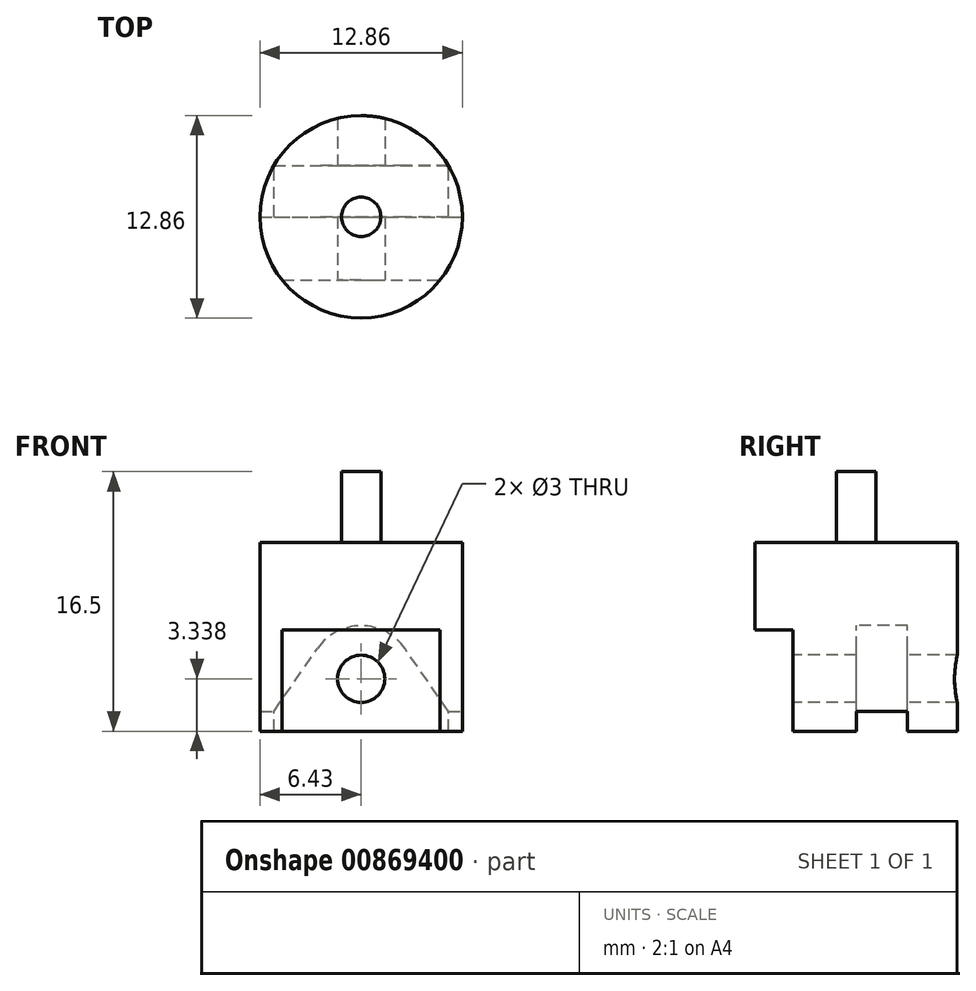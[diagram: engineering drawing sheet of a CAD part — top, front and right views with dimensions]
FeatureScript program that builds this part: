
annotation { "Feature Type Name" : "Feature", "Feature Type Description" : "" }
export const myFeature = defineFeature(function(context is Context, id is Id, definition is map)
    precondition{}
    {
        {
            var Q0;
            Q0=qCreatedBy(makeId("Top.planeOp"),FACE);
            var sketch = newSketch(context, id + "F0", { "sketchPlane" : qUnion([Q0])});
            skCircle(sketch, "E0", {"center": v(0, 0) * mm, "radius": 6.42 * mm});
            skSolve(sketch);
        }
        {
            var Q0;
            Q0=qSketchRegion(id+"F0",true);
            extrude(context, id + "F1", {"entities" : qUnion([Q0]), "oppositeDirection" : true, "depth" : 12 * mm, "offsetDistance" : 25 * mm});
        }
        {
            var Q0;
            Q0=qCreatedBy(makeId("Front.planeOp"),FACE);
            var sketch = newSketch(context, id + "F2", { "sketchPlane" : qUnion([Q0])});
            skCircle(sketch, "E1", {"center": v(0, -8.66) * mm, "radius": 1.5 * mm});
            skSolve(sketch);
        }
        {
            var Q0;
            Q0=qSketchRegion(id+"F2",true);
            extrude(context, id + "F3", {"entities" : qUnion([Q0]), "operationType" : NewBodyOperationType.REMOVE, "endBound" : BoundingType.SYMMETRIC, "oppositeDirection" : true, "depth" : 25 * mm, "offsetDistance" : 25 * mm});
        }
        {
            var Q0;
            Q0=qCreatedBy(makeId("Front.planeOp"),FACE);
            var sketch = newSketch(context, id + "F4", { "sketchPlane" : qUnion([Q0])});
            skArc(sketch, "E2", {"start": v(2.77, -6.74) * mm, "mid": v(0, -5.29) * mm, "end": v(-2.77, -6.74) * mm});
            skLineSegment(sketch, "E3.0", {"start": v(-6.42, -12) * mm, "end": v(6.42, -12) * mm});
            skLineSegment(sketch, "E4", {"start": v(6.43, -12) * mm, "end": v(2.77, -6.74) * mm});
            skLineSegment(sketch, "E5", {"start": v(-6.43, -12) * mm, "end": v(-2.77, -6.74) * mm});
            skSolve(sketch);
        }
        {
            var Q0;
            Q0=qSketchRegion(id+"F4",true);
            extrude(context, id + "F5", {"entities" : qUnion([Q0]), "operationType" : NewBodyOperationType.REMOVE, "oppositeDirection" : true, "depth" : 3.25 * mm, "offsetDistance" : 25 * mm});
        }
        {
            var Q0;
            Q0=qCreatedBy(makeId("Right.planeOp"),FACE);
            var sketch = newSketch(context, id + "F6", { "sketchPlane" : qUnion([Q0])});
            skLineSegment(sketch, "E6", {"start": v(-6.42, -12) * mm, "end": v(-6.42, -5.56) * mm});
            skLineSegment(sketch, "E7", {"start": v(-4.03, -12) * mm, "end": v(-4.03, -5.56) * mm});
            skLineSegment(sketch, "E8", {"start": v(-4.03, -5.56) * mm, "end": v(-6.42, -5.56) * mm});
            skLineSegment(sketch, "E9", {"start": v(-6.42, -7.16) * mm, "end": v(-4.03, -7.16) * mm});
            skLineSegment(sketch, "E10", {"start": v(-4.03, -10.16) * mm, "end": v(-6.42, -10.16) * mm});
            skPoint(sketch, "E11.orphan", {"position": v(-6.42, -12) * mm});
            skPoint(sketch, "E12.0.start.orphan", {"position": v(0, -12) * mm});
            skPoint(sketch, "E13.orphan", {"position": v(0, -10.16) * mm});
            skPoint(sketch, "E14.orphan", {"position": v(0, -7.16) * mm});
            skLineSegment(sketch, "E15", {"start": v(-6.42, -10.16) * mm, "end": v(-6.42, -12) * mm});
            skLineSegment(sketch, "E16", {"start": v(-4.03, -12) * mm, "end": v(-6.42, -12) * mm});
            skLineSegment(sketch, "E17.0", {"start": v(0, -10.73) * mm, "end": v(0, -12) * mm});
            skLineSegment(sketch, "E18.0", {"start": v(3.25, -10.73) * mm, "end": v(3.25, -12) * mm});
            skLineSegment(sketch, "E19", {"start": v(0, -10.73) * mm, "end": v(3.25, -10.73) * mm});
            skLineSegment(sketch, "E20", {"start": v(0, -12) * mm, "end": v(3.25, -12) * mm});
            skSolve(sketch);
        }
        {
            var Q0;
            {var subQ0=sQuery(id+"F6.wireOp",EDGE,"E10");var subQ6=makeQuery(id+"F6.imprint","IMPRINT",EDGE,{"derivedFrom":subQ0});var subQ7=sQuery(id+"F6.wireOp",EDGE,"E9");var subQ10=makeQuery(id+"F6.imprint","IMPRINT",EDGE,{"derivedFrom":subQ7});var subQ11=sQuery(id+"F6.wireOp",EDGE,"E8");Q0=qUnion([makeQuery(id+"F6.imprint","IMPRINT",FACE,{"disambiguationData":[TD([[makeQuery(id+"F6.imprint","IMPRINT",EDGE,{"derivedFrom":sQuery(id+"F6.wireOp",EDGE,"E17.0")}),1.0]])]}),makeQuery(id+"F6.imprint","IMPRINT",FACE,{"disambiguationData":[TD([[makeQuery(id+"F6.imprint","IMPRINT",EDGE,{"derivedFrom":subQ11}),1.0]])]}),makeQuery(id+"F6.imprint","IMPRINT",FACE,{"disambiguationData":[TD([[subQ10,-1.0]])]}),makeQuery(id+"F6.imprint","IMPRINT",FACE,{"disambiguationData":[TD([[subQ6,1.0]])]})]);}
            extrude(context, id + "F7", {"entities" : qUnion([Q0]), "operationType" : NewBodyOperationType.REMOVE, "endBound" : BoundingType.SYMMETRIC, "oppositeDirection" : true, "depth" : 25 * mm, "offsetDistance" : 25 * mm});
        }
        {
            var Q0;
            Q0=makeQuery(id+"F1.opExtrude","CAP_FACE",FACE,{"disambiguationData":[OSD([sQuery(id+"F0.wireOp",EDGE,"E0")])],"isStart":true});
            var sketch = newSketch(context, id + "F8", { "sketchPlane" : qUnion([Q0])});
            skCircle(sketch, "E21", {"center": v(0, 0) * mm, "radius": 1.25 * mm});
            skSolve(sketch);
        }
        {
            var Q0;
            Q0=makeQuery(id+"F8.imprint","IMPRINT",FACE,{"disambiguationData":[TD([[makeQuery(id+"F8.imprint","IMPRINT",EDGE,{"derivedFrom":sQuery(id+"F8.wireOp",EDGE,"E21")}),1.0]])]});
            extrude(context, id + "F9", {"entities" : qUnion([Q0]), "operationType" : NewBodyOperationType.ADD, "depth" : 4.5 * mm, "offsetDistance" : 25 * mm});
        }
    });
